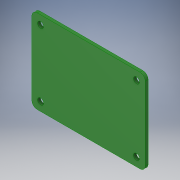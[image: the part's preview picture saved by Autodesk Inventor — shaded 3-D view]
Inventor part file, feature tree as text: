
AUTODESK INVENTOR PART (.ipt)
format: ipt  version: 2019.4 (Build 234330000, 330)  size: 122,880 bytes
history: native  units: mm
features: extrude x1, sketch x1, imported_body x1
ambient origin geometry x8: Origin, YZ Plane, XZ Plane, XY Plane, X Axis, Y Axis, Z Axis, Center Point
bodies: Solid1 (feature_tree)
feature tree (3):
  extrude  "Extrusion1"  Depth=3.0mm
  sketch  "Sketch1"  dims[d0=3.5mm d1=5.0mm d2=5.0mm d3=3.5mm d4=3.5mm d5=3.5mm d6=5.0mm d7=5.0mm d8=5.0mm d9=5.0mm d10=5.0mm d11=5.0mm d12=3.0mm d13=0.0mm]
  imported_body  "Base1"
